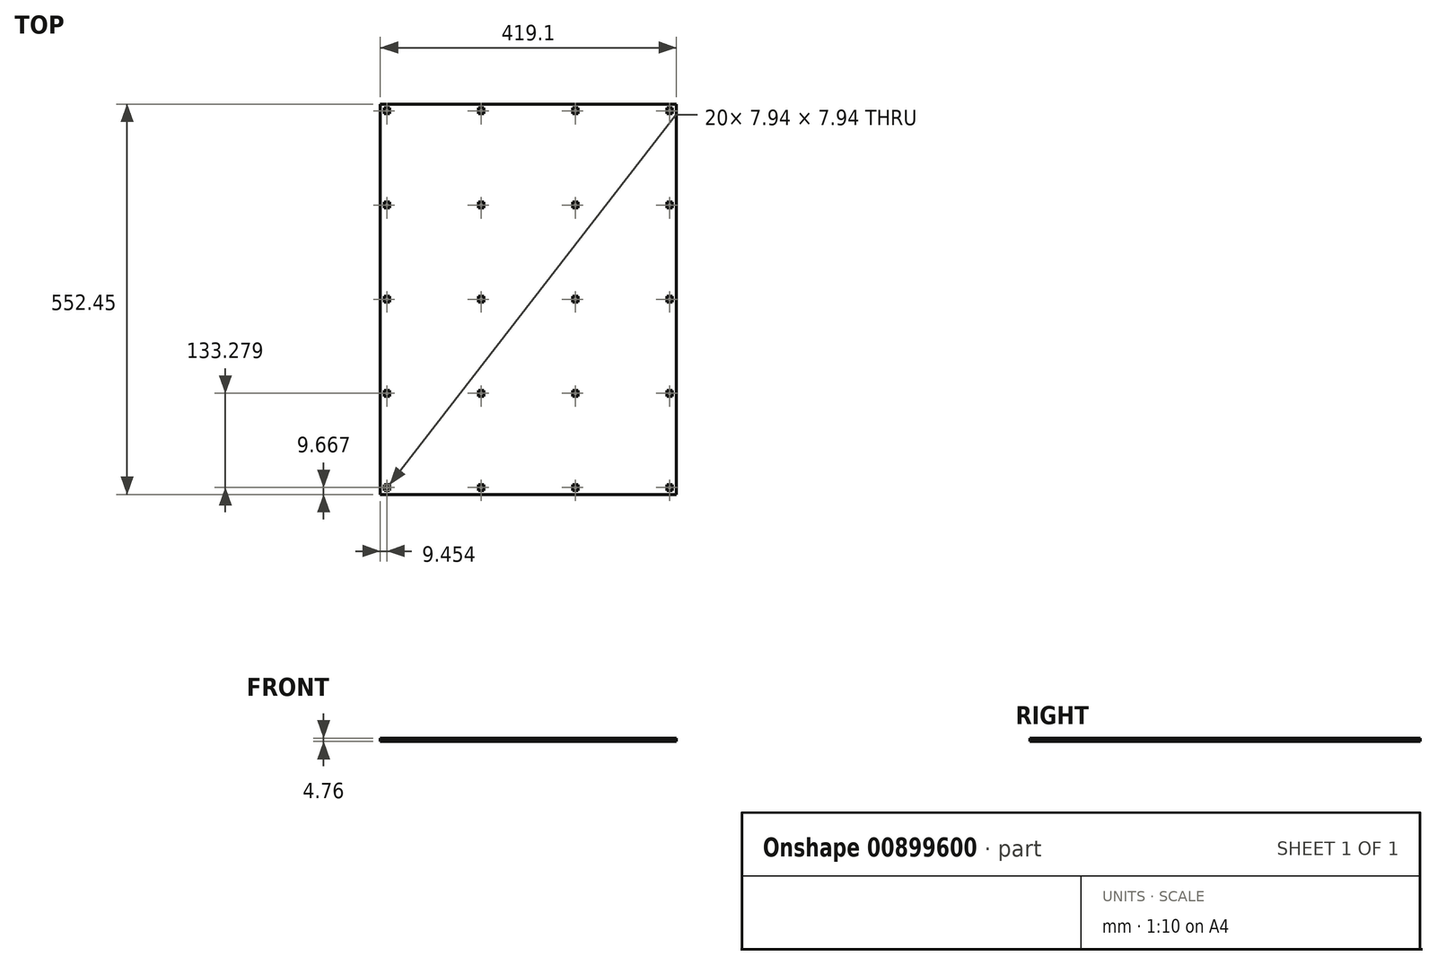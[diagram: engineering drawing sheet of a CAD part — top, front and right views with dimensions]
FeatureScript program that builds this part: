
annotation { "Feature Type Name" : "Feature", "Feature Type Description" : "" }
export const myFeature = defineFeature(function(context is Context, id is Id, definition is map)
    precondition{}
    {
        {
            var Q0;
            Q0=qCreatedBy(makeId("Top.planeOp"),FACE);
            var sketch = newSketch(context, id + "F0", { "sketchPlane" : qUnion([Q0])});
            skLineSegment(sketch, "E0.bottom", {"start": v(19.05, 12.84) * mm, "end": v(133.35, 12.84) * mm, "construction": true});
            skLineSegment(sketch, "E0.top", {"start": v(19.05, 139.84) * mm, "end": v(133.35, 139.84) * mm, "construction": true});
            skLineSegment(sketch, "E0.left", {"start": v(12.7, 19.2) * mm, "end": v(12.7, 133.5) * mm, "construction": true});
            skLineSegment(sketch, "E0.right", {"start": v(139.7, 19.2) * mm, "end": v(139.7, 133.5) * mm, "construction": true});
            skArc(sketch, "E1.filletArc", {"start": v(19.05, 139.84) * mm, "mid": v(14.56, 137.98) * mm, "end": v(12.7, 133.5) * mm, "construction": true});
            skArc(sketch, "E2.filletArc", {"start": v(139.7, 133.5) * mm, "mid": v(137.84, 137.98) * mm, "end": v(133.35, 139.84) * mm, "construction": true});
            skArc(sketch, "E3.filletArc", {"start": v(133.35, 12.84) * mm, "mid": v(137.84, 14.7) * mm, "end": v(139.7, 19.2) * mm, "construction": true});
            skArc(sketch, "E4.filletArc", {"start": v(12.7, 19.2) * mm, "mid": v(14.56, 14.7) * mm, "end": v(19.05, 12.84) * mm, "construction": true});
            skLineSegment(sketch, "E5.0.1.1", {"start": v(139.63, 152.47) * mm, "end": v(139.63, 266.77) * mm, "construction": true});
            skLineSegment(sketch, "E5.0.1.2", {"start": v(18.98, 146.12) * mm, "end": v(133.28, 146.12) * mm, "construction": true});
            skLineSegment(sketch, "E5.0.1.4", {"start": v(18.98, 273.12) * mm, "end": v(133.28, 273.12) * mm, "construction": true});
            skLineSegment(sketch, "E5.0.1.5", {"start": v(12.63, 152.47) * mm, "end": v(12.63, 266.77) * mm, "construction": true});
            skArc(sketch, "E5.0.1.8", {"start": v(139.63, 266.77) * mm, "mid": v(137.77, 271.26) * mm, "end": v(133.28, 273.12) * mm, "construction": true});
            skArc(sketch, "E5.0.1.9", {"start": v(18.98, 273.12) * mm, "mid": v(14.49, 271.26) * mm, "end": v(12.63, 266.77) * mm, "construction": true});
            skArc(sketch, "E5.0.1.10", {"start": v(12.63, 152.47) * mm, "mid": v(14.49, 147.98) * mm, "end": v(18.98, 146.12) * mm, "construction": true});
            skArc(sketch, "E5.0.1.11", {"start": v(133.28, 146.12) * mm, "mid": v(137.77, 147.98) * mm, "end": v(139.63, 152.47) * mm, "construction": true});
            skLineSegment(sketch, "E5.0.2.1", {"start": v(139.7, 285.75) * mm, "end": v(139.7, 400.05) * mm, "construction": true});
            skLineSegment(sketch, "E5.0.2.2", {"start": v(19.05, 279.4) * mm, "end": v(133.35, 279.4) * mm, "construction": true});
            skLineSegment(sketch, "E5.0.2.4", {"start": v(19.05, 406.4) * mm, "end": v(133.35, 406.4) * mm, "construction": true});
            skLineSegment(sketch, "E5.0.2.5", {"start": v(12.7, 285.75) * mm, "end": v(12.7, 400.05) * mm, "construction": true});
            skArc(sketch, "E5.0.2.8", {"start": v(139.7, 400.05) * mm, "mid": v(137.84, 404.54) * mm, "end": v(133.35, 406.4) * mm, "construction": true});
            skArc(sketch, "E5.0.2.9", {"start": v(19.05, 406.4) * mm, "mid": v(14.56, 404.54) * mm, "end": v(12.7, 400.05) * mm, "construction": true});
            skArc(sketch, "E5.0.2.10", {"start": v(12.7, 285.75) * mm, "mid": v(14.56, 281.26) * mm, "end": v(19.05, 279.4) * mm, "construction": true});
            skArc(sketch, "E5.0.2.11", {"start": v(133.35, 279.4) * mm, "mid": v(137.84, 281.26) * mm, "end": v(139.7, 285.75) * mm, "construction": true});
            skLineSegment(sketch, "E5.0.3.1", {"start": v(139.7, 419.1) * mm, "end": v(139.7, 533.4) * mm, "construction": true});
            skLineSegment(sketch, "E5.0.3.2", {"start": v(19.05, 412.75) * mm, "end": v(133.35, 412.75) * mm, "construction": true});
            skLineSegment(sketch, "E5.0.3.4", {"start": v(19.05, 539.75) * mm, "end": v(133.35, 539.75) * mm, "construction": true});
            skLineSegment(sketch, "E5.0.3.5", {"start": v(12.7, 419.1) * mm, "end": v(12.7, 533.4) * mm, "construction": true});
            skArc(sketch, "E5.0.3.8", {"start": v(139.7, 533.4) * mm, "mid": v(137.84, 537.9) * mm, "end": v(133.35, 539.75) * mm, "construction": true});
            skArc(sketch, "E5.0.3.9", {"start": v(19.05, 539.75) * mm, "mid": v(14.56, 537.9) * mm, "end": v(12.7, 533.4) * mm, "construction": true});
            skArc(sketch, "E5.0.3.10", {"start": v(12.7, 419.1) * mm, "mid": v(14.56, 414.6) * mm, "end": v(19.05, 412.75) * mm, "construction": true});
            skArc(sketch, "E5.0.3.11", {"start": v(133.35, 412.75) * mm, "mid": v(137.84, 414.6) * mm, "end": v(139.7, 419.1) * mm, "construction": true});
            skLineSegment(sketch, "E5.1.0.1", {"start": v(272.98, 19.12) * mm, "end": v(272.98, 133.42) * mm, "construction": true});
            skLineSegment(sketch, "E5.1.0.2", {"start": v(152.33, 12.77) * mm, "end": v(266.63, 12.77) * mm, "construction": true});
            skLineSegment(sketch, "E5.1.0.4", {"start": v(152.33, 139.77) * mm, "end": v(266.63, 139.77) * mm, "construction": true});
            skLineSegment(sketch, "E5.1.0.5", {"start": v(145.98, 19.12) * mm, "end": v(145.98, 133.42) * mm, "construction": true});
            skArc(sketch, "E5.1.0.8", {"start": v(272.98, 133.42) * mm, "mid": v(271.12, 137.91) * mm, "end": v(266.63, 139.77) * mm, "construction": true});
            skArc(sketch, "E5.1.0.9", {"start": v(152.33, 139.77) * mm, "mid": v(147.84, 137.91) * mm, "end": v(145.98, 133.42) * mm, "construction": true});
            skArc(sketch, "E5.1.0.10", {"start": v(145.98, 19.12) * mm, "mid": v(147.84, 14.63) * mm, "end": v(152.33, 12.77) * mm, "construction": true});
            skArc(sketch, "E5.1.0.11", {"start": v(266.63, 12.77) * mm, "mid": v(271.12, 14.63) * mm, "end": v(272.98, 19.12) * mm, "construction": true});
            skLineSegment(sketch, "E5.1.1.1", {"start": v(273.05, 152.54) * mm, "end": v(273.05, 266.84) * mm, "construction": true});
            skLineSegment(sketch, "E5.1.1.2", {"start": v(152.4, 146.2) * mm, "end": v(266.7, 146.2) * mm, "construction": true});
            skLineSegment(sketch, "E5.1.1.4", {"start": v(152.4, 273.2) * mm, "end": v(266.7, 273.2) * mm, "construction": true});
            skLineSegment(sketch, "E5.1.1.5", {"start": v(146.05, 152.54) * mm, "end": v(146.05, 266.84) * mm, "construction": true});
            skArc(sketch, "E5.1.1.8", {"start": v(273.05, 266.84) * mm, "mid": v(271.2, 271.33) * mm, "end": v(266.7, 273.2) * mm, "construction": true});
            skArc(sketch, "E5.1.1.9", {"start": v(152.4, 273.2) * mm, "mid": v(147.9, 271.33) * mm, "end": v(146.05, 266.84) * mm, "construction": true});
            skArc(sketch, "E5.1.1.10", {"start": v(146.05, 152.54) * mm, "mid": v(147.9, 148.05) * mm, "end": v(152.4, 146.2) * mm, "construction": true});
            skArc(sketch, "E5.1.1.11", {"start": v(266.7, 146.2) * mm, "mid": v(271.2, 148.05) * mm, "end": v(273.05, 152.54) * mm, "construction": true});
            skLineSegment(sketch, "E5.1.2.1", {"start": v(273.05, 285.75) * mm, "end": v(273.05, 400.05) * mm, "construction": true});
            skLineSegment(sketch, "E5.1.2.2", {"start": v(152.4, 279.4) * mm, "end": v(266.7, 279.4) * mm, "construction": true});
            skLineSegment(sketch, "E5.1.2.4", {"start": v(152.4, 406.4) * mm, "end": v(266.7, 406.4) * mm, "construction": true});
            skLineSegment(sketch, "E5.1.2.5", {"start": v(146.05, 285.75) * mm, "end": v(146.05, 400.05) * mm, "construction": true});
            skArc(sketch, "E5.1.2.8", {"start": v(273.05, 400.05) * mm, "mid": v(271.2, 404.54) * mm, "end": v(266.7, 406.4) * mm, "construction": true});
            skArc(sketch, "E5.1.2.9", {"start": v(152.4, 406.4) * mm, "mid": v(147.9, 404.54) * mm, "end": v(146.05, 400.05) * mm, "construction": true});
            skArc(sketch, "E5.1.2.10", {"start": v(146.05, 285.75) * mm, "mid": v(147.9, 281.26) * mm, "end": v(152.4, 279.4) * mm, "construction": true});
            skArc(sketch, "E5.1.2.11", {"start": v(266.7, 279.4) * mm, "mid": v(271.2, 281.26) * mm, "end": v(273.05, 285.75) * mm, "construction": true});
            skLineSegment(sketch, "E5.1.3.1", {"start": v(273.05, 419.1) * mm, "end": v(273.05, 533.4) * mm, "construction": true});
            skLineSegment(sketch, "E5.1.3.2", {"start": v(152.4, 412.75) * mm, "end": v(266.7, 412.75) * mm, "construction": true});
            skLineSegment(sketch, "E5.1.3.4", {"start": v(152.4, 539.75) * mm, "end": v(266.7, 539.75) * mm, "construction": true});
            skLineSegment(sketch, "E5.1.3.5", {"start": v(146.05, 419.1) * mm, "end": v(146.05, 533.4) * mm, "construction": true});
            skArc(sketch, "E5.1.3.8", {"start": v(273.05, 533.4) * mm, "mid": v(271.2, 537.9) * mm, "end": v(266.7, 539.75) * mm, "construction": true});
            skArc(sketch, "E5.1.3.9", {"start": v(152.4, 539.75) * mm, "mid": v(147.9, 537.9) * mm, "end": v(146.05, 533.4) * mm, "construction": true});
            skArc(sketch, "E5.1.3.10", {"start": v(146.05, 419.1) * mm, "mid": v(147.9, 414.6) * mm, "end": v(152.4, 412.75) * mm, "construction": true});
            skArc(sketch, "E5.1.3.11", {"start": v(266.7, 412.75) * mm, "mid": v(271.2, 414.6) * mm, "end": v(273.05, 419.1) * mm, "construction": true});
            skLineSegment(sketch, "E5.2.0.1", {"start": v(406.4, 19.05) * mm, "end": v(406.4, 133.35) * mm, "construction": true});
            skLineSegment(sketch, "E5.2.0.2", {"start": v(285.75, 12.7) * mm, "end": v(400.05, 12.7) * mm, "construction": true});
            skLineSegment(sketch, "E5.2.0.4", {"start": v(285.75, 139.7) * mm, "end": v(400.05, 139.7) * mm, "construction": true});
            skLineSegment(sketch, "E5.2.0.5", {"start": v(279.4, 19.05) * mm, "end": v(279.4, 133.35) * mm, "construction": true});
            skArc(sketch, "E5.2.0.8", {"start": v(406.4, 133.35) * mm, "mid": v(404.54, 137.84) * mm, "end": v(400.05, 139.7) * mm, "construction": true});
            skArc(sketch, "E5.2.0.9", {"start": v(285.75, 139.7) * mm, "mid": v(281.26, 137.84) * mm, "end": v(279.4, 133.35) * mm, "construction": true});
            skArc(sketch, "E5.2.0.10", {"start": v(279.4, 19.05) * mm, "mid": v(281.26, 14.56) * mm, "end": v(285.75, 12.7) * mm, "construction": true});
            skArc(sketch, "E5.2.0.11", {"start": v(400.05, 12.7) * mm, "mid": v(404.54, 14.56) * mm, "end": v(406.4, 19.05) * mm, "construction": true});
            skLineSegment(sketch, "E5.2.1.1", {"start": v(406.4, 152.4) * mm, "end": v(406.4, 266.7) * mm, "construction": true});
            skLineSegment(sketch, "E5.2.1.2", {"start": v(285.75, 146.05) * mm, "end": v(400.05, 146.05) * mm, "construction": true});
            skLineSegment(sketch, "E5.2.1.4", {"start": v(285.75, 273.05) * mm, "end": v(400.05, 273.05) * mm, "construction": true});
            skLineSegment(sketch, "E5.2.1.5", {"start": v(279.4, 152.4) * mm, "end": v(279.4, 266.7) * mm, "construction": true});
            skArc(sketch, "E5.2.1.8", {"start": v(406.4, 266.7) * mm, "mid": v(404.54, 271.2) * mm, "end": v(400.05, 273.05) * mm, "construction": true});
            skArc(sketch, "E5.2.1.9", {"start": v(285.75, 273.05) * mm, "mid": v(281.26, 271.2) * mm, "end": v(279.4, 266.7) * mm, "construction": true});
            skArc(sketch, "E5.2.1.10", {"start": v(279.4, 152.4) * mm, "mid": v(281.26, 147.9) * mm, "end": v(285.75, 146.05) * mm, "construction": true});
            skArc(sketch, "E5.2.1.11", {"start": v(400.05, 146.05) * mm, "mid": v(404.54, 147.9) * mm, "end": v(406.4, 152.4) * mm, "construction": true});
            skLineSegment(sketch, "E5.2.2.1", {"start": v(406.4, 285.75) * mm, "end": v(406.4, 400.05) * mm, "construction": true});
            skLineSegment(sketch, "E5.2.2.2", {"start": v(285.75, 279.4) * mm, "end": v(400.05, 279.4) * mm, "construction": true});
            skLineSegment(sketch, "E5.2.2.4", {"start": v(285.75, 406.4) * mm, "end": v(400.05, 406.4) * mm, "construction": true});
            skLineSegment(sketch, "E5.2.2.5", {"start": v(279.4, 285.75) * mm, "end": v(279.4, 400.05) * mm, "construction": true});
            skArc(sketch, "E5.2.2.8", {"start": v(406.4, 400.05) * mm, "mid": v(404.54, 404.54) * mm, "end": v(400.05, 406.4) * mm, "construction": true});
            skArc(sketch, "E5.2.2.9", {"start": v(285.75, 406.4) * mm, "mid": v(281.26, 404.54) * mm, "end": v(279.4, 400.05) * mm, "construction": true});
            skArc(sketch, "E5.2.2.10", {"start": v(279.4, 285.75) * mm, "mid": v(281.26, 281.26) * mm, "end": v(285.75, 279.4) * mm, "construction": true});
            skArc(sketch, "E5.2.2.11", {"start": v(400.05, 279.4) * mm, "mid": v(404.54, 281.26) * mm, "end": v(406.4, 285.75) * mm, "construction": true});
            skLineSegment(sketch, "E5.2.3.1", {"start": v(406.4, 419.1) * mm, "end": v(406.4, 533.4) * mm, "construction": true});
            skLineSegment(sketch, "E5.2.3.2", {"start": v(285.75, 412.75) * mm, "end": v(400.05, 412.75) * mm, "construction": true});
            skLineSegment(sketch, "E5.2.3.4", {"start": v(285.75, 539.75) * mm, "end": v(400.05, 539.75) * mm, "construction": true});
            skLineSegment(sketch, "E5.2.3.5", {"start": v(279.4, 419.1) * mm, "end": v(279.4, 533.4) * mm, "construction": true});
            skArc(sketch, "E5.2.3.8", {"start": v(406.4, 533.4) * mm, "mid": v(404.54, 537.9) * mm, "end": v(400.05, 539.75) * mm, "construction": true});
            skArc(sketch, "E5.2.3.9", {"start": v(285.75, 539.75) * mm, "mid": v(281.26, 537.9) * mm, "end": v(279.4, 533.4) * mm, "construction": true});
            skArc(sketch, "E5.2.3.10", {"start": v(279.4, 419.1) * mm, "mid": v(281.26, 414.6) * mm, "end": v(285.75, 412.75) * mm, "construction": true});
            skArc(sketch, "E5.2.3.11", {"start": v(400.05, 412.75) * mm, "mid": v(404.54, 414.6) * mm, "end": v(406.4, 419.1) * mm, "construction": true});
            skLineSegment(sketch, "E6.bottom", {"start": v(0, 0) * mm, "end": v(419.1, 0) * mm});
            skLineSegment(sketch, "E6.top", {"start": v(0, 552.45) * mm, "end": v(419.1, 552.45) * mm});
            skLineSegment(sketch, "E6.left", {"start": v(0, 0) * mm, "end": v(0, 552.45) * mm});
            skLineSegment(sketch, "E6.right", {"start": v(419.1, 0) * mm, "end": v(419.1, 552.45) * mm});
            skLineSegment(sketch, "E7", {"start": v(133.28, 152.47) * mm, "end": v(152.33, 133.42) * mm, "construction": true});
            skLineSegment(sketch, "E8", {"start": v(152.4, 152.54) * mm, "end": v(133.35, 133.5) * mm, "construction": true});
            skLineSegment(sketch, "E9.bottom", {"start": v(13.42, 13.64) * mm, "end": v(5.49, 13.64) * mm});
            skLineSegment(sketch, "E9.top", {"start": v(13.42, 5.7) * mm, "end": v(5.49, 5.7) * mm});
            skLineSegment(sketch, "E9.left", {"start": v(13.42, 13.64) * mm, "end": v(13.42, 5.7) * mm});
            skLineSegment(sketch, "E9.right", {"start": v(5.49, 13.64) * mm, "end": v(5.49, 5.7) * mm});
            skPoint(sketch, "E9.middle", {"position": v(142.8, 142.95) * mm});
            skCircle(sketch, "E10", {"center": v(9.45, 9.67) * mm, "radius": 3.97 * mm, "construction": true});
            skLineSegment(sketch, "E11", {"start": v(266.63, 133.42) * mm, "end": v(285.75, 152.4) * mm, "construction": true});
            skLineSegment(sketch, "E12", {"start": v(285.75, 133.35) * mm, "end": v(266.7, 152.54) * mm, "construction": true});
            skLineSegment(sketch, "E13", {"start": v(133.35, 285.75) * mm, "end": v(152.4, 266.84) * mm, "construction": true});
            skLineSegment(sketch, "E14", {"start": v(133.28, 266.77) * mm, "end": v(152.4, 285.75) * mm, "construction": true});
            skLineSegment(sketch, "E15", {"start": v(266.7, 285.75) * mm, "end": v(285.75, 266.7) * mm, "construction": true});
            skLineSegment(sketch, "E16", {"start": v(285.75, 285.75) * mm, "end": v(266.7, 266.84) * mm, "construction": true});
            skLineSegment(sketch, "E17", {"start": v(142.84, 276.26) * mm, "end": v(276.19, 276.26) * mm, "construction": true});
            skLineSegment(sketch, "E18", {"start": v(276.19, 276.26) * mm, "end": v(276.19, 142.98) * mm, "construction": true});
            skLineSegment(sketch, "E19.0.1.0", {"start": v(13.42, 138.98) * mm, "end": v(5.49, 138.98) * mm});
            skLineSegment(sketch, "E19.0.1.1", {"start": v(13.42, 146.91) * mm, "end": v(5.49, 146.91) * mm});
            skLineSegment(sketch, "E19.0.1.2", {"start": v(5.49, 146.91) * mm, "end": v(5.49, 138.98) * mm});
            skLineSegment(sketch, "E19.0.1.3", {"start": v(13.42, 146.91) * mm, "end": v(13.42, 138.98) * mm});
            skCircle(sketch, "E19.0.1.4", {"center": v(9.45, 142.95) * mm, "radius": 3.97 * mm, "construction": true});
            skLineSegment(sketch, "E19.1.0.0", {"start": v(146.77, 5.7) * mm, "end": v(138.84, 5.7) * mm});
            skLineSegment(sketch, "E19.1.0.1", {"start": v(146.77, 13.64) * mm, "end": v(138.84, 13.64) * mm});
            skLineSegment(sketch, "E19.1.0.2", {"start": v(138.84, 13.64) * mm, "end": v(138.84, 5.7) * mm});
            skLineSegment(sketch, "E19.1.0.3", {"start": v(146.77, 13.64) * mm, "end": v(146.77, 5.7) * mm});
            skCircle(sketch, "E19.1.0.4", {"center": v(142.8, 9.67) * mm, "radius": 3.97 * mm, "construction": true});
            skLineSegment(sketch, "E19.1.1.0", {"start": v(146.77, 138.98) * mm, "end": v(138.84, 138.98) * mm});
            skLineSegment(sketch, "E19.1.1.1", {"start": v(146.77, 146.91) * mm, "end": v(138.84, 146.91) * mm});
            skLineSegment(sketch, "E19.1.1.2", {"start": v(138.84, 146.91) * mm, "end": v(138.84, 138.98) * mm});
            skLineSegment(sketch, "E19.1.1.3", {"start": v(146.77, 146.91) * mm, "end": v(146.77, 138.98) * mm});
            skCircle(sketch, "E19.1.1.4", {"center": v(142.8, 142.95) * mm, "radius": 3.97 * mm, "construction": true});
            skLineSegment(sketch, "E19.2.0.0", {"start": v(280.12, 5.7) * mm, "end": v(272.19, 5.7) * mm});
            skLineSegment(sketch, "E19.2.0.1", {"start": v(280.12, 13.64) * mm, "end": v(272.19, 13.64) * mm});
            skLineSegment(sketch, "E19.2.0.2", {"start": v(272.19, 13.64) * mm, "end": v(272.19, 5.7) * mm});
            skLineSegment(sketch, "E19.2.0.3", {"start": v(280.12, 13.64) * mm, "end": v(280.12, 5.7) * mm});
            skCircle(sketch, "E19.2.0.4", {"center": v(276.15, 9.67) * mm, "radius": 3.97 * mm, "construction": true});
            skLineSegment(sketch, "E19.2.1.0", {"start": v(280.12, 138.98) * mm, "end": v(272.19, 138.98) * mm});
            skLineSegment(sketch, "E19.2.1.1", {"start": v(280.12, 146.91) * mm, "end": v(272.19, 146.91) * mm});
            skLineSegment(sketch, "E19.2.1.2", {"start": v(272.19, 146.91) * mm, "end": v(272.19, 138.98) * mm});
            skLineSegment(sketch, "E19.2.1.3", {"start": v(280.12, 146.91) * mm, "end": v(280.12, 138.98) * mm});
            skCircle(sketch, "E19.2.1.4", {"center": v(276.15, 142.95) * mm, "radius": 3.97 * mm, "construction": true});
            skLineSegment(sketch, "E19.3.0.0", {"start": v(413.47, 5.7) * mm, "end": v(405.54, 5.7) * mm});
            skLineSegment(sketch, "E19.3.0.1", {"start": v(413.47, 13.64) * mm, "end": v(405.54, 13.64) * mm});
            skLineSegment(sketch, "E19.3.0.2", {"start": v(405.54, 13.64) * mm, "end": v(405.54, 5.7) * mm});
            skLineSegment(sketch, "E19.3.0.3", {"start": v(413.47, 13.64) * mm, "end": v(413.47, 5.7) * mm});
            skCircle(sketch, "E19.3.0.4", {"center": v(409.5, 9.67) * mm, "radius": 3.97 * mm, "construction": true});
            skLineSegment(sketch, "E19.3.1.0", {"start": v(413.47, 138.98) * mm, "end": v(405.54, 138.98) * mm});
            skLineSegment(sketch, "E19.3.1.1", {"start": v(413.47, 146.91) * mm, "end": v(405.54, 146.91) * mm});
            skLineSegment(sketch, "E19.3.1.2", {"start": v(405.54, 146.91) * mm, "end": v(405.54, 138.98) * mm});
            skLineSegment(sketch, "E19.3.1.3", {"start": v(413.47, 146.91) * mm, "end": v(413.47, 138.98) * mm});
            skCircle(sketch, "E19.3.1.4", {"center": v(409.5, 142.95) * mm, "radius": 3.97 * mm, "construction": true});
            skLineSegment(sketch, "E19.direction1", {"start": v(5.49, 5.7) * mm, "end": v(138.84, 5.7) * mm, "construction": true});
            skLineSegment(sketch, "E19.direction2", {"start": v(5.49, 5.7) * mm, "end": v(5.49, 138.98) * mm, "construction": true});
            skLineSegment(sketch, "E20.0.0.2", {"start": v(13.42, 272.26) * mm, "end": v(5.49, 272.26) * mm});
            skLineSegment(sketch, "E20.3.0.2", {"start": v(13.42, 280.2) * mm, "end": v(5.49, 280.2) * mm});
            skLineSegment(sketch, "E20.6.0.2", {"start": v(5.49, 280.2) * mm, "end": v(5.49, 272.26) * mm});
            skLineSegment(sketch, "E20.9.0.2", {"start": v(13.42, 280.2) * mm, "end": v(13.42, 272.26) * mm});
            skCircle(sketch, "E20.12.0.2", {"center": v(9.45, 276.22) * mm, "radius": 3.97 * mm, "construction": true});
            skLineSegment(sketch, "E20.0.0.3", {"start": v(13.42, 405.53) * mm, "end": v(5.49, 405.53) * mm});
            skLineSegment(sketch, "E20.3.0.3", {"start": v(13.42, 413.47) * mm, "end": v(5.49, 413.47) * mm});
            skLineSegment(sketch, "E20.6.0.3", {"start": v(5.49, 413.47) * mm, "end": v(5.49, 405.53) * mm});
            skLineSegment(sketch, "E20.9.0.3", {"start": v(13.42, 413.47) * mm, "end": v(13.42, 405.53) * mm});
            skCircle(sketch, "E20.12.0.3", {"center": v(9.45, 409.5) * mm, "radius": 3.97 * mm, "construction": true});
            skLineSegment(sketch, "E20.0.0.4", {"start": v(13.42, 538.81) * mm, "end": v(5.49, 538.81) * mm});
            skLineSegment(sketch, "E20.3.0.4", {"start": v(13.42, 546.75) * mm, "end": v(5.49, 546.75) * mm});
            skLineSegment(sketch, "E20.6.0.4", {"start": v(5.49, 546.75) * mm, "end": v(5.49, 538.81) * mm});
            skLineSegment(sketch, "E20.9.0.4", {"start": v(13.42, 546.75) * mm, "end": v(13.42, 538.81) * mm});
            skCircle(sketch, "E20.12.0.4", {"center": v(9.45, 542.78) * mm, "radius": 3.97 * mm, "construction": true});
            skLineSegment(sketch, "E20.0.1.2", {"start": v(146.77, 272.26) * mm, "end": v(138.84, 272.26) * mm});
            skLineSegment(sketch, "E20.3.1.2", {"start": v(146.77, 280.2) * mm, "end": v(138.84, 280.2) * mm});
            skLineSegment(sketch, "E20.6.1.2", {"start": v(138.84, 280.2) * mm, "end": v(138.84, 272.26) * mm});
            skLineSegment(sketch, "E20.9.1.2", {"start": v(146.77, 280.2) * mm, "end": v(146.77, 272.26) * mm});
            skCircle(sketch, "E20.12.1.2", {"center": v(142.8, 276.22) * mm, "radius": 3.97 * mm, "construction": true});
            skLineSegment(sketch, "E20.0.1.3", {"start": v(146.77, 405.53) * mm, "end": v(138.84, 405.53) * mm});
            skLineSegment(sketch, "E20.3.1.3", {"start": v(146.77, 413.47) * mm, "end": v(138.84, 413.47) * mm});
            skLineSegment(sketch, "E20.6.1.3", {"start": v(138.84, 413.47) * mm, "end": v(138.84, 405.53) * mm});
            skLineSegment(sketch, "E20.9.1.3", {"start": v(146.77, 413.47) * mm, "end": v(146.77, 405.53) * mm});
            skCircle(sketch, "E20.12.1.3", {"center": v(142.8, 409.5) * mm, "radius": 3.97 * mm, "construction": true});
            skLineSegment(sketch, "E20.0.1.4", {"start": v(146.77, 538.81) * mm, "end": v(138.84, 538.81) * mm});
            skLineSegment(sketch, "E20.3.1.4", {"start": v(146.77, 546.75) * mm, "end": v(138.84, 546.75) * mm});
            skLineSegment(sketch, "E20.6.1.4", {"start": v(138.84, 546.75) * mm, "end": v(138.84, 538.81) * mm});
            skLineSegment(sketch, "E20.9.1.4", {"start": v(146.77, 546.75) * mm, "end": v(146.77, 538.81) * mm});
            skCircle(sketch, "E20.12.1.4", {"center": v(142.8, 542.78) * mm, "radius": 3.97 * mm, "construction": true});
            skLineSegment(sketch, "E20.0.2.2", {"start": v(280.12, 272.26) * mm, "end": v(272.19, 272.26) * mm});
            skLineSegment(sketch, "E20.3.2.2", {"start": v(280.12, 280.2) * mm, "end": v(272.19, 280.2) * mm});
            skLineSegment(sketch, "E20.6.2.2", {"start": v(272.19, 280.2) * mm, "end": v(272.19, 272.26) * mm});
            skLineSegment(sketch, "E20.9.2.2", {"start": v(280.12, 280.2) * mm, "end": v(280.12, 272.26) * mm});
            skCircle(sketch, "E20.12.2.2", {"center": v(276.15, 276.22) * mm, "radius": 3.97 * mm, "construction": true});
            skLineSegment(sketch, "E20.0.2.3", {"start": v(280.12, 405.53) * mm, "end": v(272.19, 405.53) * mm});
            skLineSegment(sketch, "E20.3.2.3", {"start": v(280.12, 413.47) * mm, "end": v(272.19, 413.47) * mm});
            skLineSegment(sketch, "E20.6.2.3", {"start": v(272.19, 413.47) * mm, "end": v(272.19, 405.53) * mm});
            skLineSegment(sketch, "E20.9.2.3", {"start": v(280.12, 413.47) * mm, "end": v(280.12, 405.53) * mm});
            skCircle(sketch, "E20.12.2.3", {"center": v(276.15, 409.5) * mm, "radius": 3.97 * mm, "construction": true});
            skLineSegment(sketch, "E20.0.2.4", {"start": v(280.12, 538.81) * mm, "end": v(272.19, 538.81) * mm});
            skLineSegment(sketch, "E20.3.2.4", {"start": v(280.12, 546.75) * mm, "end": v(272.19, 546.75) * mm});
            skLineSegment(sketch, "E20.6.2.4", {"start": v(272.19, 546.75) * mm, "end": v(272.19, 538.81) * mm});
            skLineSegment(sketch, "E20.9.2.4", {"start": v(280.12, 546.75) * mm, "end": v(280.12, 538.81) * mm});
            skCircle(sketch, "E20.12.2.4", {"center": v(276.15, 542.78) * mm, "radius": 3.97 * mm, "construction": true});
            skLineSegment(sketch, "E20.0.3.2", {"start": v(413.47, 272.26) * mm, "end": v(405.54, 272.26) * mm});
            skLineSegment(sketch, "E20.3.3.2", {"start": v(413.47, 280.2) * mm, "end": v(405.54, 280.2) * mm});
            skLineSegment(sketch, "E20.6.3.2", {"start": v(405.54, 280.2) * mm, "end": v(405.54, 272.26) * mm});
            skLineSegment(sketch, "E20.9.3.2", {"start": v(413.47, 280.2) * mm, "end": v(413.47, 272.26) * mm});
            skCircle(sketch, "E20.12.3.2", {"center": v(409.5, 276.22) * mm, "radius": 3.97 * mm, "construction": true});
            skLineSegment(sketch, "E20.0.3.3", {"start": v(413.47, 405.53) * mm, "end": v(405.54, 405.53) * mm});
            skLineSegment(sketch, "E20.3.3.3", {"start": v(413.47, 413.47) * mm, "end": v(405.54, 413.47) * mm});
            skLineSegment(sketch, "E20.6.3.3", {"start": v(405.54, 413.47) * mm, "end": v(405.54, 405.53) * mm});
            skLineSegment(sketch, "E20.9.3.3", {"start": v(413.47, 413.47) * mm, "end": v(413.47, 405.53) * mm});
            skCircle(sketch, "E20.12.3.3", {"center": v(409.5, 409.5) * mm, "radius": 3.97 * mm, "construction": true});
            skLineSegment(sketch, "E20.0.3.4", {"start": v(413.47, 538.81) * mm, "end": v(405.54, 538.81) * mm});
            skLineSegment(sketch, "E20.3.3.4", {"start": v(413.47, 546.75) * mm, "end": v(405.54, 546.75) * mm});
            skLineSegment(sketch, "E20.6.3.4", {"start": v(405.54, 546.75) * mm, "end": v(405.54, 538.81) * mm});
            skLineSegment(sketch, "E20.9.3.4", {"start": v(413.47, 546.75) * mm, "end": v(413.47, 538.81) * mm});
            skCircle(sketch, "E20.12.3.4", {"center": v(409.5, 542.78) * mm, "radius": 3.97 * mm, "construction": true});
            skSolve(sketch);
        }
        {
            var Q0;
            Q0=makeQuery(id+"F0.imprint","IMPRINT",FACE,{"disambiguationData":[TD([[makeQuery(id+"F0.imprint","IMPRINT",EDGE,{"derivedFrom":sQuery(id+"F0.wireOp",EDGE,"E6.bottom")}),1.0]])]});
            extrude(context, id + "F1", {"entities" : qUnion([Q0]), "depth" : 4.76 * mm, "offsetDistance" : 25.4 * mm});
        }
    });
